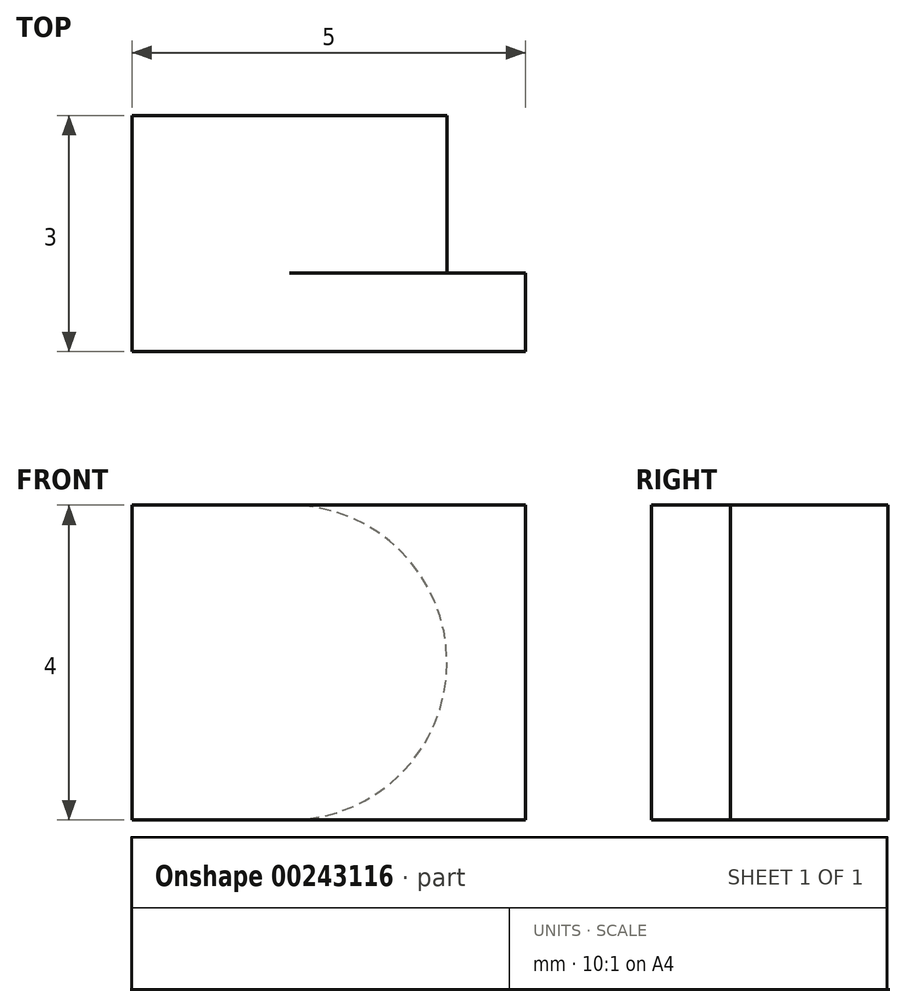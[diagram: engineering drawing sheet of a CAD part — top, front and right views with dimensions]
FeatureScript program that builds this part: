
annotation { "Feature Type Name" : "Feature", "Feature Type Description" : "" }
export const myFeature = defineFeature(function(context is Context, id is Id, definition is map)
    precondition{}
    {
        {
            var Q0;
            Q0=qCreatedBy(makeId("Top.planeOp"),FACE);
            var sketch = newSketch(context, id + "F0", { "sketchPlane" : qUnion([Q0])});
            skLineSegment(sketch, "E0", {"start": v(0, 0) * mm, "end": v(5, 0) * mm});
            skLineSegment(sketch, "E1", {"start": v(5, 0) * mm, "end": v(5, 3) * mm});
            skLineSegment(sketch, "E2", {"start": v(5, 3) * mm, "end": v(0, 3) * mm});
            skLineSegment(sketch, "E3", {"start": v(0, 3) * mm, "end": v(0, 0) * mm});
            skSolve(sketch);
        }
        {
            var Q0;
            Q0=makeQuery(id+"F0.imprint","IMPRINT",FACE,{"disambiguationData":[TD([[makeQuery(id+"F0.imprint","IMPRINT",EDGE,{"derivedFrom":sQuery(id+"F0.wireOp",EDGE,"E0")}),1.0]])]});
            extrude(context, id + "F1", {"entities" : qUnion([Q0]), "depth" : 4 * mm});
        }
        {
            var Q0;
            Q0=makeQuery(id+"F1.opExtrude","SWEPT_FACE",FACE,{"disambiguationData":[OSD([sQuery(id+"F0.wireOp",EDGE,"E2")])]});
            var sketch = newSketch(context, id + "F2", { "sketchPlane" : qUnion([Q0])});
            skLineSegment(sketch, "E4", {"start": v(0, 0) * mm, "end": v(-2, 0) * mm});
            skPoint(sketch, "E5.endSnap0", {"position": v(-2.5, 4) * mm});
            skLineSegment(sketch, "E6", {"start": v(-2, 0) * mm, "end": v(-2, 2) * mm});
            skCircle(sketch, "E7", {"center": v(-2, 2) * mm, "radius": 2 * mm});
            skSolve(sketch);
        }
        {
            var Q0;
            {var subQ1=sQuery(id+"F0.wireOp",EDGE,"E2");var subQ6=makeQuery(id+"F1.opExtrude","SWEPT_EDGE",EDGE,{"disambiguationData":[OSD([sQuery(id+"F0.wireOp",EDGE,"E1"),subQ1])]});Q0=makeQuery(id+"F2.imprint","IMPRINT",FACE,{"disambiguationData":[TD([[makeQuery(id+"F2.imprint","IMPRINT",EDGE,{"derivedFrom":subQ6}),1.0]])]});}
            extrude(context, id + "F3", {"entities" : qUnion([Q0]), "operationType" : NewBodyOperationType.REMOVE, "oppositeDirection" : true, "depth" : 2 * mm});
        }
    });
